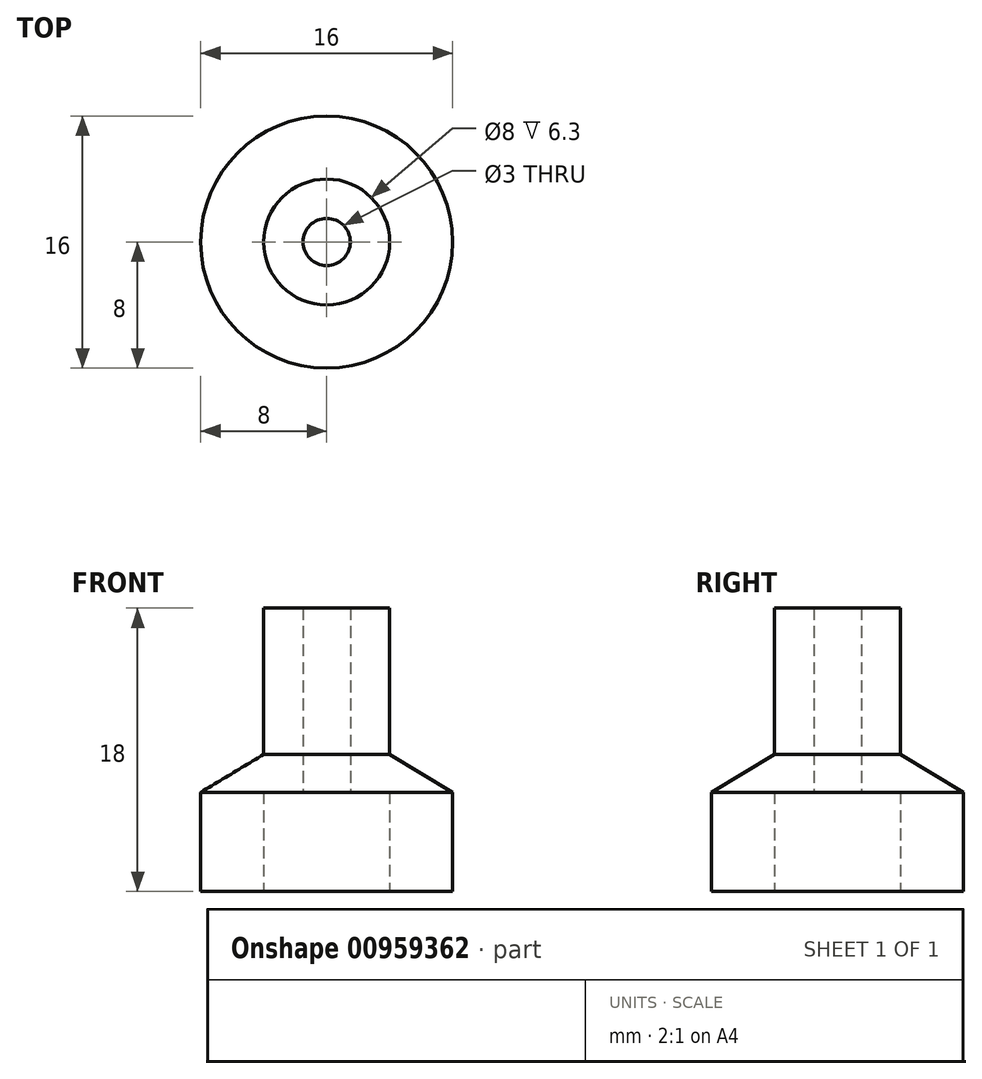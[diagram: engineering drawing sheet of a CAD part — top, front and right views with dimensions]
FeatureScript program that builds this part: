
annotation { "Feature Type Name" : "Feature", "Feature Type Description" : "" }
export const myFeature = defineFeature(function(context is Context, id is Id, definition is map)
    precondition{}
    {
        {
            var Q0;
            Q0=qCreatedBy(makeId("Top.planeOp"),FACE);
            var sketch = newSketch(context, id + "F0", { "sketchPlane" : qUnion([Q0])});
            skCircle(sketch, "E0", {"center": v(0, 0) * mm, "radius": 8 * mm});
            skCircle(sketch, "E1", {"center": v(0, 0) * mm, "radius": 4 * mm});
            skCircle(sketch, "E2", {"center": v(0, 0) * mm, "radius": 1.5 * mm});
            skSolve(sketch);
        }
        {
            var Q0;
            Q0=qCreatedBy(makeId("Front.planeOp"),FACE);
            var sketch = newSketch(context, id + "F1", { "sketchPlane" : qUnion([Q0])});
            skLineSegment(sketch, "E3.left", {"start": v(-8, 0) * mm, "end": v(-8, 6.3) * mm});
            skLineSegment(sketch, "E3.right", {"start": v(8, 0) * mm, "end": v(8, 6.3) * mm});
            skLineSegment(sketch, "E4.left", {"start": v(-4, 8.7) * mm, "end": v(-4, 18) * mm});
            skLineSegment(sketch, "E4.right", {"start": v(4, 8.7) * mm, "end": v(4, 18) * mm});
            skLineSegment(sketch, "E5", {"start": v(-8, 6.3) * mm, "end": v(-4, 8.7) * mm});
            skLineSegment(sketch, "E6", {"start": v(4, 8.7) * mm, "end": v(8, 6.3) * mm});
            skLineSegment(sketch, "E7", {"start": v(-8, 0) * mm, "end": v(-4, 0) * mm});
            skLineSegment(sketch, "E8", {"start": v(4, 6.3) * mm, "end": v(4, 0) * mm});
            skLineSegment(sketch, "E9", {"start": v(4, 0) * mm, "end": v(8, 0) * mm});
            skLineSegment(sketch, "E10", {"start": v(-4, 6.3) * mm, "end": v(-4, 0) * mm});
            skLineSegment(sketch, "E11", {"start": v(-1.5, 18) * mm, "end": v(-1.5, 6.3) * mm});
            skLineSegment(sketch, "E12", {"start": v(1.5, 18) * mm, "end": v(1.5, 6.3) * mm});
            skLineSegment(sketch, "E13", {"start": v(-4, 18) * mm, "end": v(-1.5, 18) * mm});
            skLineSegment(sketch, "E14", {"start": v(1.5, 18) * mm, "end": v(4, 18) * mm});
            skLineSegment(sketch, "E15", {"start": v(-1.5, 18) * mm, "end": v(1.5, 18) * mm, "construction": true});
            skLineSegment(sketch, "E16", {"start": v(-4, 6.3) * mm, "end": v(-1.5, 6.3) * mm});
            skLineSegment(sketch, "E17", {"start": v(1.5, 6.3) * mm, "end": v(4, 6.3) * mm});
            skLineSegment(sketch, "E18", {"start": v(-4, 6.3) * mm, "end": v(4, 6.3) * mm, "construction": true});
            skLineSegment(sketch, "E19", {"start": v(-4, 18) * mm, "end": v(4, 18) * mm, "construction": true});
            skSolve(sketch);
        }
        {
            var Q0;
            Q0=makeQuery(id+"F1.imprint","IMPRINT",FACE,{"disambiguationData":[TD([[makeQuery(id+"F1.imprint","IMPRINT",EDGE,{"derivedFrom":sQuery(id+"F1.wireOp",EDGE,"E3.left")}),-1.0]])]});
            var Q1;
            Q1=sQuery(id+"F0.wireOp",EDGE,"E2");
            revolve(context, id + "F2", {"surfaceOperationType" : NewSurfaceOperationType.NEW, "entities" : qUnion([Q0]), "axis" : qUnion([Q1]), "revolveType" : RevolveType.SYMMETRIC, "angle" : 360 * degree});
        }
    });
